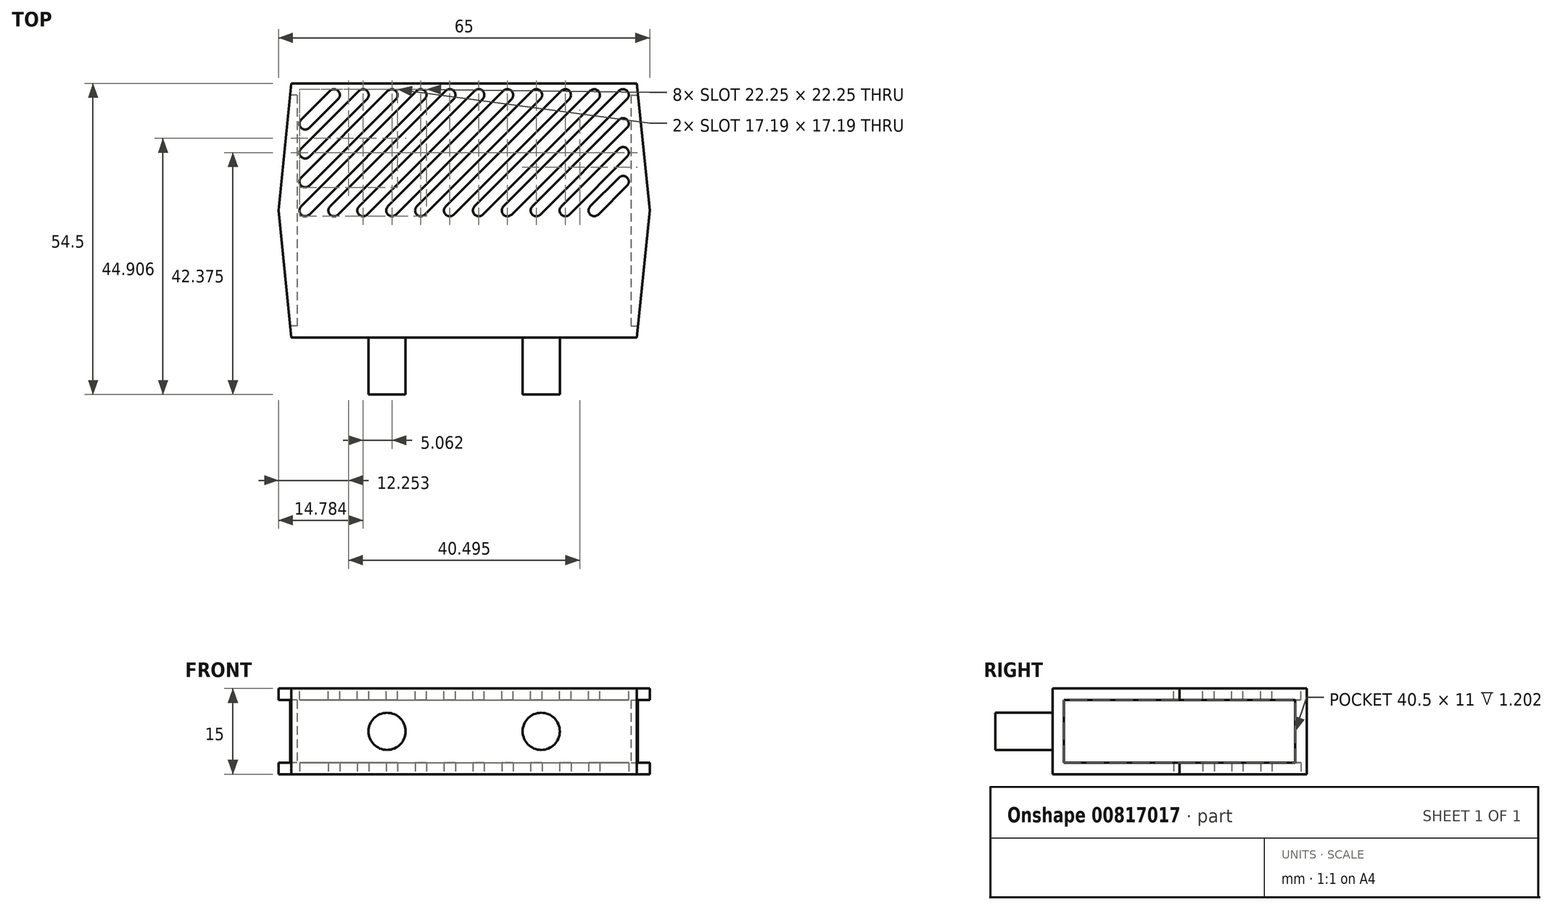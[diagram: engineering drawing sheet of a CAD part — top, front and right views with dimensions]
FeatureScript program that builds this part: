
annotation { "Feature Type Name" : "Feature", "Feature Type Description" : "" }
export const myFeature = defineFeature(function(context is Context, id is Id, definition is map)
    precondition{}
    {
        {
            var Q0;
            Q0=qCreatedBy(makeId("Top.planeOp"),FACE);
            var sketch = newSketch(context, id + "F0", { "sketchPlane" : qUnion([Q0])});
            skLineSegment(sketch, "E0.bottom", {"start": v(-29.25, 20.25) * mm, "end": v(29.25, 20.25) * mm});
            skLineSegment(sketch, "E0.top", {"start": v(-29.25, -20.25) * mm, "end": v(29.25, -20.25) * mm});
            skLineSegment(sketch, "E0.left", {"start": v(-29.25, 20.25) * mm, "end": v(-29.25, -20.25) * mm});
            skLineSegment(sketch, "E0.right", {"start": v(29.25, 20.25) * mm, "end": v(29.25, -20.25) * mm});
            skPoint(sketch, "E0.middle", {"position": v(0, 0) * mm});
            skLineSegment(sketch, "E1.bottom", {"start": v(-30.25, 22.25) * mm, "end": v(30.25, 22.25) * mm});
            skLineSegment(sketch, "E1.top", {"start": v(-30.25, -22.25) * mm, "end": v(30.25, -22.25) * mm});
            skLineSegment(sketch, "E1.left", {"start": v(-30.25, 22.25) * mm, "end": v(-30.25, -22.25) * mm, "construction": true});
            skLineSegment(sketch, "E1.right", {"start": v(30.25, 22.25) * mm, "end": v(30.25, -22.25) * mm, "construction": true});
            skLineSegment(sketch, "E2", {"start": v(-30.25, 22.25) * mm, "end": v(-32.5, 0) * mm});
            skLineSegment(sketch, "E3", {"start": v(-32.5, 0) * mm, "end": v(-30.25, -22.25) * mm});
            skLineSegment(sketch, "E4", {"start": v(30.25, -22.25) * mm, "end": v(32.5, 0) * mm});
            skLineSegment(sketch, "E5", {"start": v(32.5, 0) * mm, "end": v(30.25, 22.25) * mm});
            skLineSegment(sketch, "E6", {"start": v(-29.25, -20.25) * mm, "end": v(-30.45, -20.25) * mm});
            skLineSegment(sketch, "E7", {"start": v(-29.25, 20.25) * mm, "end": v(-30.45, 20.25) * mm});
            skLineSegment(sketch, "E8", {"start": v(29.25, 20.25) * mm, "end": v(30.45, 20.25) * mm});
            skLineSegment(sketch, "E9", {"start": v(29.25, -20.25) * mm, "end": v(30.45, -20.25) * mm});
            skSolve(sketch);
        }
        {
            var Q0;
            Q0=makeQuery(id+"F0.imprint","IMPRINT",FACE,{"disambiguationData":[TD([[makeQuery(id+"F0.imprint","IMPRINT",EDGE,{"derivedFrom":sQuery(id+"F0.wireOp",EDGE,"E0.bottom")}),-1.0]])]});
            var Q1;
            Q1=makeQuery(id+"F0.imprint","IMPRINT",FACE,{"disambiguationData":[TD([[makeQuery(id+"F0.imprint","IMPRINT",EDGE,{"derivedFrom":sQuery(id+"F0.wireOp",EDGE,"E0.left")}),-1.0]])]});
            var Q2;
            Q2=makeQuery(id+"F0.imprint","IMPRINT",FACE,{"disambiguationData":[TD([[makeQuery(id+"F0.imprint","IMPRINT",EDGE,{"derivedFrom":sQuery(id+"F0.wireOp",EDGE,"E0.bottom")}),1.0]])]});
            var Q3;
            Q3=makeQuery(id+"F0.imprint","IMPRINT",FACE,{"disambiguationData":[TD([[makeQuery(id+"F0.imprint","IMPRINT",EDGE,{"derivedFrom":sQuery(id+"F0.wireOp",EDGE,"E0.right")}),1.0]])]});
            var Q4;
            Q4=makeQuery(id+"F0.imprint","IMPRINT",FACE,{"disambiguationData":[TD([[makeQuery(id+"F0.imprint","IMPRINT",EDGE,{"derivedFrom":sQuery(id+"F0.wireOp",EDGE,"E0.top")}),-1.0]])]});
            extrude(context, id + "F1", {"entities" : qUnion([Q0, Q1, Q2, Q3, Q4]), "endBound" : BoundingType.SYMMETRIC, "depth" : 15 * mm});
        }
        {
            var Q0;
            Q0=makeQuery(id+"F0.imprint","IMPRINT",FACE,{"disambiguationData":[TD([[makeQuery(id+"F0.imprint","IMPRINT",EDGE,{"derivedFrom":sQuery(id+"F0.wireOp",EDGE,"E0.left")}),-1.0]])]});
            var Q1;
            Q1=makeQuery(id+"F0.imprint","IMPRINT",FACE,{"disambiguationData":[TD([[makeQuery(id+"F0.imprint","IMPRINT",EDGE,{"derivedFrom":sQuery(id+"F0.wireOp",EDGE,"E0.right")}),1.0]])]});
            extrude(context, id + "F2", {"entities" : qUnion([Q0, Q1]), "operationType" : NewBodyOperationType.REMOVE, "endBound" : BoundingType.SYMMETRIC, "depth" : 11 * mm});
        }
        {
            var Q0;
            Q0=makeQuery(id+"F1.opExtrude","CAP_FACE",FACE,{"disambiguationData":[OSD([sQuery(id+"F0.wireOp",EDGE,"E1.bottom"),sQuery(id+"F0.wireOp",EDGE,"E1.top"),sQuery(id+"F0.wireOp",EDGE,"E2"),sQuery(id+"F0.wireOp",EDGE,"E3"),sQuery(id+"F0.wireOp",EDGE,"E4"),sQuery(id+"F0.wireOp",EDGE,"E5")])],"isStart":false});
            var sketch = newSketch(context, id + "F3", { "sketchPlane" : qUnion([Q0])});
            skLineSegment(sketch, "E10.bottom", {"start": v(-27.84, 20.25) * mm, "end": v(27.84, 20.25) * mm, "construction": true});
            skLineSegment(sketch, "E10.top", {"start": v(-27.84, 0) * mm, "end": v(27.84, 0) * mm, "construction": true});
            skLineSegment(sketch, "E10.left", {"start": v(-27.84, 20.25) * mm, "end": v(-27.84, 0) * mm, "construction": true});
            skLineSegment(sketch, "E10.right", {"start": v(27.84, 20.25) * mm, "end": v(27.84, 0) * mm, "construction": true});
            skPoint(sketch, "E10.middle", {"position": v(0, 10.12) * mm});
            skLineSegment(sketch, "E11", {"start": v(-17.72, 20.25) * mm, "end": v(-27.84, 10.12) * mm});
            skLineSegment(sketch, "E12", {"start": v(-12.65, 20.25) * mm, "end": v(-27.84, 5.06) * mm});
            skLineSegment(sketch, "E13", {"start": v(-27.84, 0) * mm, "end": v(-7.6, 20.25) * mm});
            skLineSegment(sketch, "E14", {"start": v(-27.84, 15.19) * mm, "end": v(-22.78, 20.25) * mm});
            skLineSegment(sketch, "E15", {"start": v(-25.3, 17.72) * mm, "end": v(-20.25, 17.72) * mm, "construction": true});
            skLineSegment(sketch, "E16", {"start": v(-20.25, 17.72) * mm, "end": v(-15.19, 17.72) * mm, "construction": true});
            skLineSegment(sketch, "E17", {"start": v(-15.19, 17.72) * mm, "end": v(-10.12, 17.72) * mm, "construction": true});
            skLineSegment(sketch, "E18.1.0.0", {"start": v(-22.78, 0) * mm, "end": v(-2.53, 20.25) * mm});
            skLineSegment(sketch, "E18.2.0.0", {"start": v(-17.72, 0) * mm, "end": v(2.53, 20.25) * mm});
            skLineSegment(sketch, "E18.3.0.0", {"start": v(-12.66, 0) * mm, "end": v(7.6, 20.25) * mm});
            skLineSegment(sketch, "E18.4.0.0", {"start": v(-7.6, 0) * mm, "end": v(12.66, 20.25) * mm});
            skLineSegment(sketch, "E18.5.0.0", {"start": v(-2.53, 0) * mm, "end": v(17.72, 20.25) * mm});
            skLineSegment(sketch, "E18.6.0.0", {"start": v(2.53, 0) * mm, "end": v(22.78, 20.25) * mm});
            skLineSegment(sketch, "E18.7.0.0", {"start": v(7.6, 0) * mm, "end": v(27.84, 20.25) * mm});
            skLineSegment(sketch, "E18.direction1", {"start": v(-27.84, 0) * mm, "end": v(-22.78, 0) * mm, "construction": true});
            skLineSegment(sketch, "E19", {"start": v(-10.12, 17.72) * mm, "end": v(-5.06, 17.72) * mm, "construction": true});
            skLineSegment(sketch, "E20.1.0", {"start": v(12.65, 0) * mm, "end": v(27.84, 15.19) * mm});
            skLineSegment(sketch, "E20.1.1", {"start": v(17.72, 0) * mm, "end": v(27.84, 10.13) * mm});
            skLineSegment(sketch, "E20.1.2", {"start": v(27.84, 5.06) * mm, "end": v(22.78, 0) * mm});
            skArc(sketch, "E21.0.startCap", {"start": v(-27.13, 14.48) * mm, "mid": v(-28.55, 14.48) * mm, "end": v(-28.55, 15.9) * mm});
            skArc(sketch, "E21.0.endCap", {"start": v(-23.48, 20.96) * mm, "mid": v(-22.07, 20.96) * mm, "end": v(-22.07, 19.54) * mm});
            skLineSegment(sketch, "E21.0.left", {"start": v(-28.55, 15.9) * mm, "end": v(-23.48, 20.96) * mm});
            skLineSegment(sketch, "E21.0.right", {"start": v(-27.13, 14.48) * mm, "end": v(-22.07, 19.54) * mm});
            skArc(sketch, "E22.0.startCap", {"start": v(-18.42, 20.96) * mm, "mid": v(-17, 20.96) * mm, "end": v(-17, 19.54) * mm});
            skArc(sketch, "E22.0.endCap", {"start": v(-27.13, 9.42) * mm, "mid": v(-28.55, 9.42) * mm, "end": v(-28.55, 10.83) * mm});
            skLineSegment(sketch, "E22.0.left", {"start": v(-17, 19.54) * mm, "end": v(-27.13, 9.42) * mm});
            skLineSegment(sketch, "E22.0.right", {"start": v(-18.42, 20.96) * mm, "end": v(-28.55, 10.83) * mm});
            skArc(sketch, "E22.1.startCap", {"start": v(-13.36, 20.96) * mm, "mid": v(-11.95, 20.96) * mm, "end": v(-11.95, 19.54) * mm});
            skArc(sketch, "E22.1.endCap", {"start": v(-27.13, 4.35) * mm, "mid": v(-28.55, 4.35) * mm, "end": v(-28.55, 5.77) * mm});
            skLineSegment(sketch, "E22.1.left", {"start": v(-11.95, 19.54) * mm, "end": v(-27.13, 4.35) * mm});
            skLineSegment(sketch, "E22.1.right", {"start": v(-13.36, 20.96) * mm, "end": v(-28.55, 5.77) * mm});
            skArc(sketch, "E22.2.startCap", {"start": v(-27.13, -0.7) * mm, "mid": v(-28.55, -0.7) * mm, "end": v(-28.55, 0.7) * mm});
            skArc(sketch, "E22.2.endCap", {"start": v(-8.3, 20.96) * mm, "mid": v(-6.88, 20.96) * mm, "end": v(-6.88, 19.54) * mm});
            skLineSegment(sketch, "E22.2.left", {"start": v(-28.55, 0.7) * mm, "end": v(-8.3, 20.96) * mm});
            skLineSegment(sketch, "E22.2.right", {"start": v(-27.13, -0.7) * mm, "end": v(-6.88, 19.54) * mm});
            skArc(sketch, "E22.3.startCap", {"start": v(-22.07, -0.7) * mm, "mid": v(-23.49, -0.7) * mm, "end": v(-23.49, 0.7) * mm});
            skArc(sketch, "E22.3.endCap", {"start": v(-3.24, 20.96) * mm, "mid": v(-1.82, 20.96) * mm, "end": v(-1.82, 19.54) * mm});
            skLineSegment(sketch, "E22.3.left", {"start": v(-23.49, 0.7) * mm, "end": v(-3.24, 20.96) * mm});
            skLineSegment(sketch, "E22.3.right", {"start": v(-22.07, -0.7) * mm, "end": v(-1.82, 19.54) * mm});
            skArc(sketch, "E22.4.startCap", {"start": v(-17.01, -0.7) * mm, "mid": v(-18.42, -0.7) * mm, "end": v(-18.42, 0.7) * mm});
            skArc(sketch, "E22.4.endCap", {"start": v(1.83, 20.96) * mm, "mid": v(3.24, 20.96) * mm, "end": v(3.24, 19.54) * mm});
            skLineSegment(sketch, "E22.4.left", {"start": v(-18.42, 0.7) * mm, "end": v(1.83, 20.96) * mm});
            skLineSegment(sketch, "E22.4.right", {"start": v(-17.01, -0.7) * mm, "end": v(3.24, 19.54) * mm});
            skArc(sketch, "E22.5.startCap", {"start": v(-11.95, -0.7) * mm, "mid": v(-13.36, -0.7) * mm, "end": v(-13.36, 0.7) * mm});
            skArc(sketch, "E22.5.endCap", {"start": v(6.89, 20.96) * mm, "mid": v(8.3, 20.96) * mm, "end": v(8.3, 19.54) * mm});
            skLineSegment(sketch, "E22.5.left", {"start": v(-13.36, 0.7) * mm, "end": v(6.89, 20.96) * mm});
            skLineSegment(sketch, "E22.5.right", {"start": v(-11.95, -0.7) * mm, "end": v(8.3, 19.54) * mm});
            skArc(sketch, "E22.6.startCap", {"start": v(-6.89, -0.7) * mm, "mid": v(-8.3, -0.7) * mm, "end": v(-8.3, 0.7) * mm});
            skArc(sketch, "E22.6.endCap", {"start": v(11.95, 20.96) * mm, "mid": v(13.36, 20.96) * mm, "end": v(13.36, 19.54) * mm});
            skLineSegment(sketch, "E22.6.left", {"start": v(-8.3, 0.7) * mm, "end": v(11.95, 20.96) * mm});
            skLineSegment(sketch, "E22.6.right", {"start": v(-6.89, -0.7) * mm, "end": v(13.36, 19.54) * mm});
            skArc(sketch, "E22.7.startCap", {"start": v(-1.83, -0.7) * mm, "mid": v(-3.24, -0.7) * mm, "end": v(-3.24, 0.7) * mm});
            skArc(sketch, "E22.7.endCap", {"start": v(17.01, 20.96) * mm, "mid": v(18.42, 20.96) * mm, "end": v(18.42, 19.54) * mm});
            skLineSegment(sketch, "E22.7.left", {"start": v(-3.24, 0.7) * mm, "end": v(17.01, 20.96) * mm});
            skLineSegment(sketch, "E22.7.right", {"start": v(-1.83, -0.7) * mm, "end": v(18.42, 19.54) * mm});
            skArc(sketch, "E22.8.startCap", {"start": v(3.24, -0.7) * mm, "mid": v(1.82, -0.7) * mm, "end": v(1.82, 0.7) * mm});
            skArc(sketch, "E22.8.endCap", {"start": v(22.07, 20.96) * mm, "mid": v(23.49, 20.96) * mm, "end": v(23.49, 19.54) * mm});
            skLineSegment(sketch, "E22.8.left", {"start": v(1.82, 0.7) * mm, "end": v(22.07, 20.96) * mm});
            skLineSegment(sketch, "E22.8.right", {"start": v(3.24, -0.7) * mm, "end": v(23.49, 19.54) * mm});
            skArc(sketch, "E22.9.startCap", {"start": v(8.3, -0.7) * mm, "mid": v(6.88, -0.7) * mm, "end": v(6.88, 0.7) * mm});
            skArc(sketch, "E22.9.endCap", {"start": v(27.13, 20.96) * mm, "mid": v(28.55, 20.96) * mm, "end": v(28.55, 19.54) * mm});
            skLineSegment(sketch, "E22.9.left", {"start": v(6.88, 0.7) * mm, "end": v(27.13, 20.96) * mm});
            skLineSegment(sketch, "E22.9.right", {"start": v(8.3, -0.7) * mm, "end": v(28.55, 19.54) * mm});
            skArc(sketch, "E22.10.startCap", {"start": v(13.36, -0.7) * mm, "mid": v(11.95, -0.7) * mm, "end": v(11.95, 0.7) * mm});
            skArc(sketch, "E22.10.endCap", {"start": v(27.13, 15.9) * mm, "mid": v(28.55, 15.9) * mm, "end": v(28.55, 14.48) * mm});
            skLineSegment(sketch, "E22.10.left", {"start": v(11.95, 0.7) * mm, "end": v(27.13, 15.9) * mm});
            skLineSegment(sketch, "E22.10.right", {"start": v(13.36, -0.7) * mm, "end": v(28.55, 14.48) * mm});
            skArc(sketch, "E22.11.startCap", {"start": v(18.42, -0.7) * mm, "mid": v(17, -0.7) * mm, "end": v(17, 0.7) * mm});
            skArc(sketch, "E22.11.endCap", {"start": v(27.13, 10.83) * mm, "mid": v(28.55, 10.83) * mm, "end": v(28.55, 9.42) * mm});
            skLineSegment(sketch, "E22.11.left", {"start": v(17, 0.7) * mm, "end": v(27.13, 10.83) * mm});
            skLineSegment(sketch, "E22.11.right", {"start": v(18.42, -0.7) * mm, "end": v(28.55, 9.42) * mm});
            skArc(sketch, "E22.12.startCap", {"start": v(27.13, 5.77) * mm, "mid": v(28.55, 5.77) * mm, "end": v(28.55, 4.36) * mm});
            skArc(sketch, "E22.12.endCap", {"start": v(23.48, -0.7) * mm, "mid": v(22.07, -0.7) * mm, "end": v(22.07, 0.7) * mm});
            skLineSegment(sketch, "E22.12.left", {"start": v(28.55, 4.36) * mm, "end": v(23.48, -0.7) * mm});
            skLineSegment(sketch, "E22.12.right", {"start": v(27.13, 5.77) * mm, "end": v(22.07, 0.7) * mm});
            skSolve(sketch);
        }
        {
            var Q0;
            Q0=qSketchRegion(id+"F3",true);
            extrude(context, id + "F4", {"entities" : qUnion([Q0]), "operationType" : NewBodyOperationType.REMOVE, "oppositeDirection" : true, "depth" : 2 * mm});
        }
        {
            var Q0;
            Q0=makeQuery(id+"F1.opExtrude","SWEPT_BODY",BODY,{"disambiguationData":[OSD([sQuery(id+"F0.wireOp",EDGE,"E1.bottom"),sQuery(id+"F0.wireOp",EDGE,"E1.top"),sQuery(id+"F0.wireOp",EDGE,"E2"),sQuery(id+"F0.wireOp",EDGE,"E3"),sQuery(id+"F0.wireOp",EDGE,"E4"),sQuery(id+"F0.wireOp",EDGE,"E5")])]});
            var Q1;
            Q1=qCreatedBy(makeId("Top.planeOp"),FACE);
            mirror(context, id + "F5", {"operationType" : NewBodyOperationType.INTERSECT, "entities" : qUnion([Q0]), "mirrorPlane" : qUnion([Q1])});
        }
        {
            var Q0;
            Q0=makeQuery(id+"F1.opExtrude","SWEPT_FACE",FACE,{"disambiguationData":[OSD([sQuery(id+"F0.wireOp",EDGE,"E1.top")])]});
            var sketch = newSketch(context, id + "F6", { "sketchPlane" : qUnion([Q0])});
            skCircle(sketch, "E23", {"center": v(-13.5, 0) * mm, "radius": 3.25 * mm});
            skLineSegment(sketch, "E24", {"start": v(0, 0) * mm, "end": v(0, 7.5) * mm, "construction": true});
            skCircle(sketch, "E25.MirrorC", {"center": v(13.5, 0) * mm, "radius": 3.25 * mm});
            skSolve(sketch);
        }
        {
            var Q0;
            Q0=qSketchRegion(id+"F6",true);
            extrude(context, id + "F7", {"entities" : qUnion([Q0]), "operationType" : NewBodyOperationType.ADD, "depth" : 10 * mm});
        }
    });
